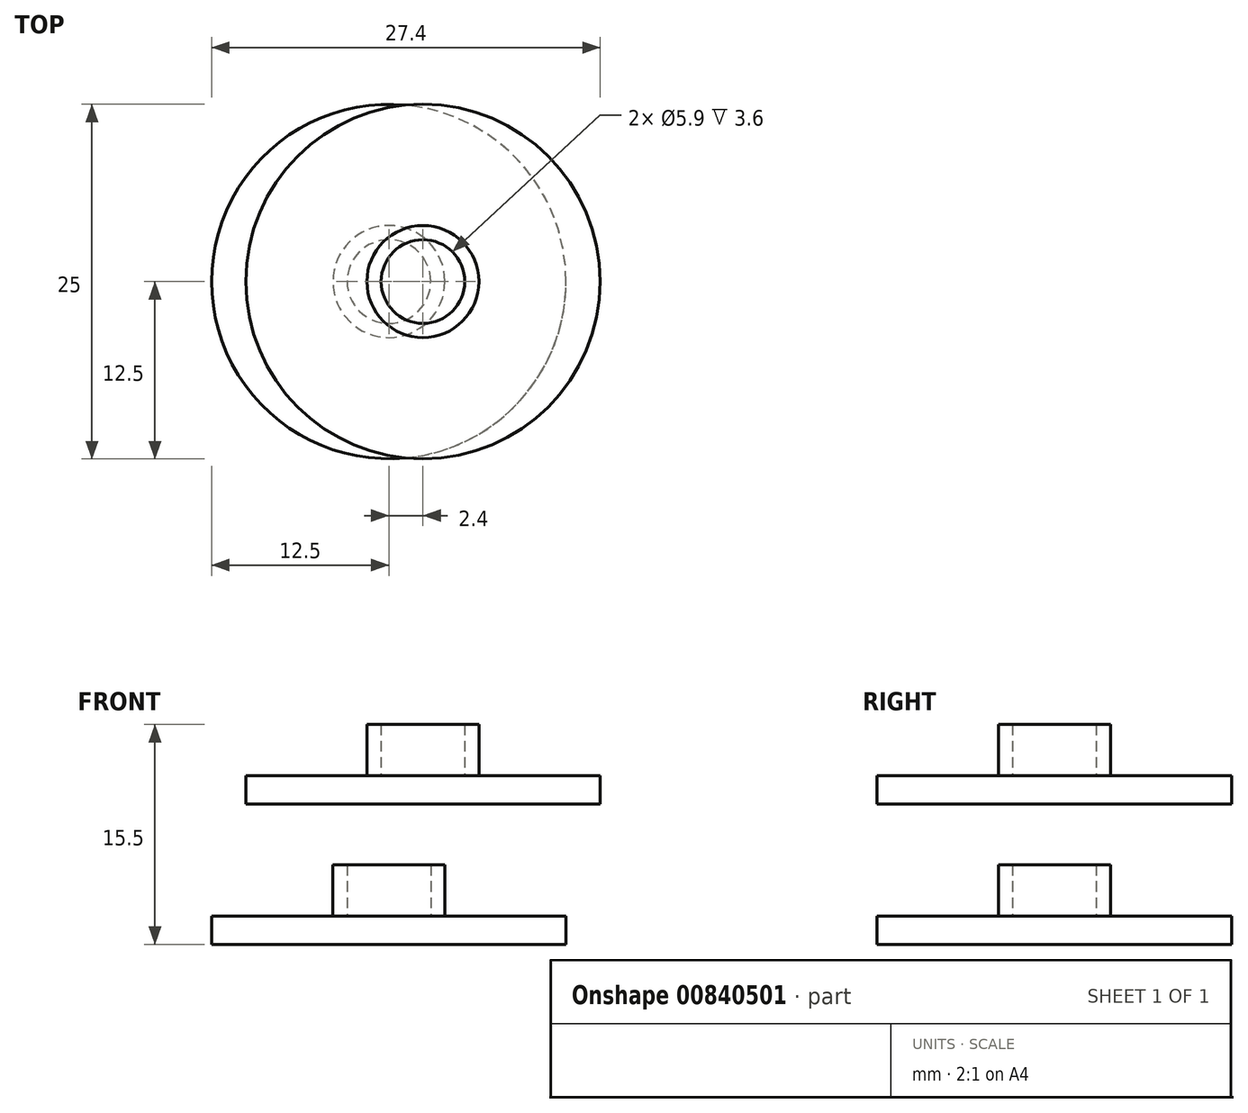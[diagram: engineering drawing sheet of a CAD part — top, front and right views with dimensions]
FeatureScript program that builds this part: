
annotation { "Feature Type Name" : "Feature", "Feature Type Description" : "" }
export const myFeature = defineFeature(function(context is Context, id is Id, definition is map)
    precondition{}
    {
        {
            var Q0;
            Q0=qCreatedBy(makeId("Top.planeOp"),FACE);
            var sketch = newSketch(context, id + "F0", { "sketchPlane" : qUnion([Q0])});
            skCircle(sketch, "E0", {"center": v(0, 0) * mm, "radius": 12.5 * mm});
            skSolve(sketch);
        }
        {
            var Q0;
            Q0 = qSketchRegion(id + "F0", true);
            extrude(context, id + "F1", {"entities" : qUnion([Q0]), "endBound" : BoundingType.SYMMETRIC, "depth" : 2 * mm, "offsetDistance" : 25 * mm});
        }
        {
            var Q0;
            Q0=makeQuery(id+"F1.opExtrude","CAP_FACE",FACE,{"disambiguationData":[OSD([sQuery(id+"F0.wireOp",EDGE,"E0")])],"isStart":false});
            var sketch = newSketch(context, id + "F2", { "sketchPlane" : qUnion([Q0])});
            skCircle(sketch, "E1", {"center": v(0, 0) * mm, "radius": 3.95 * mm});
            skCircle(sketch, "E2.0", {"center": v(0, 0) * mm, "radius": 2.95 * mm});
            skSolve(sketch);
        }
        {
            var Q0;
            Q0 = qSketchRegion(id + "F2", true);
            extrude(context, id + "F3", {"entities" : qUnion([Q0]), "operationType" : NewBodyOperationType.ADD, "depth" : 3.6 * mm, "offsetDistance" : 25 * mm});
        }
        {
            var Q0;
            Q0=makeQuery(id+"F1.opExtrude","SWEPT_BODY",BODY,{"disambiguationData":[OSD([sQuery(id+"F0.wireOp",EDGE,"E0")])]});
            transform(context, id + "F4", {"entities" : qUnion([Q0]), "transformType" : TransformType.TRANSLATION_3D, "dx" : 2.4 * mm, "dy" : 0 * mm, "dz" : 9.9 * mm, "makeCopy" : true});
        }
    });
